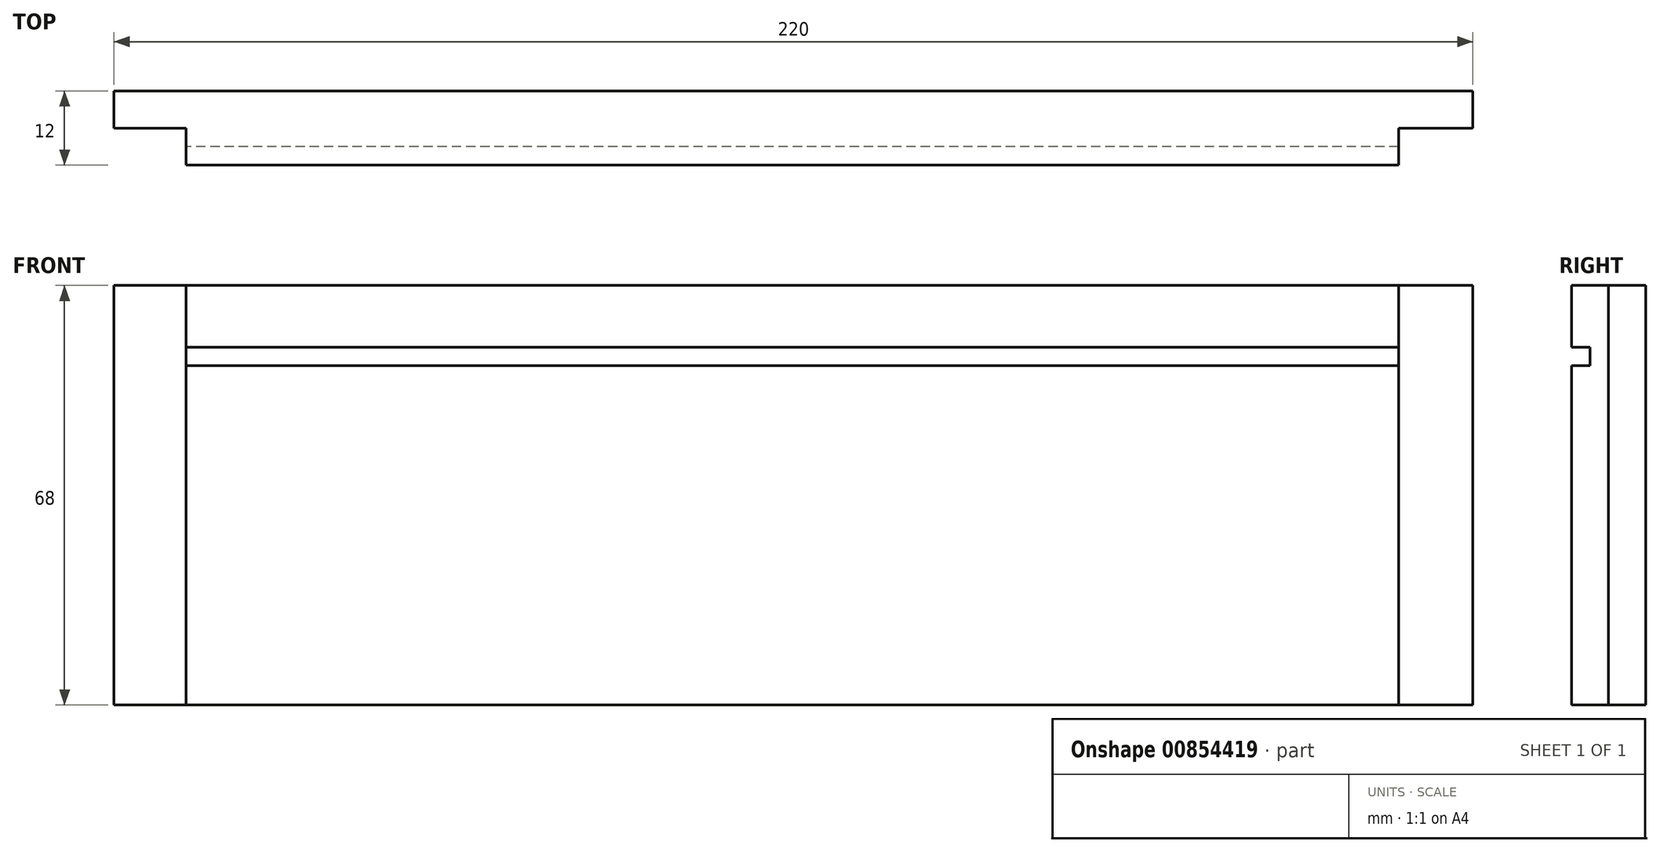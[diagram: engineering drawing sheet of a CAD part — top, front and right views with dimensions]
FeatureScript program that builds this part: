
annotation { "Feature Type Name" : "Feature", "Feature Type Description" : "" }
export const myFeature = defineFeature(function(context is Context, id is Id, definition is map)
    precondition{}
    {
        {
            var Q0;
            Q0=qCreatedBy(makeId("Front.planeOp"),FACE);
            var sketch = newSketch(context, id + "F0", { "sketchPlane" : qUnion([Q0])});
            skLineSegment(sketch, "E0.bottom", {"start": v(-110, 34) * mm, "end": v(110, 34) * mm});
            skLineSegment(sketch, "E0.top", {"start": v(-110, -34) * mm, "end": v(110, -34) * mm});
            skLineSegment(sketch, "E0.left", {"start": v(-110, 34) * mm, "end": v(-110, -34) * mm});
            skLineSegment(sketch, "E0.right", {"start": v(110, 34) * mm, "end": v(110, -34) * mm});
            skPoint(sketch, "E0.middle", {"position": v(0, 0) * mm});
            skSolve(sketch);
        }
        {
            var Q0;
            Q0 = qSketchRegion(id + "F0", true);
            extrude(context, id + "F1", {"entities" : qUnion([Q0]), "depth" : 12 * mm, "offsetDistance" : 25.4 * mm});
        }
        {
            var Q0;
            Q0=makeQuery(id+"F1.opExtrude","SWEPT_FACE",FACE,{"disambiguationData":[OSD([sQuery(id+"F0.wireOp",EDGE,"E0.left")])]});
            var sketch = newSketch(context, id + "F2", { "sketchPlane" : qUnion([Q0])});
            skLineSegment(sketch, "E1.bottom", {"start": v(12, 24) * mm, "end": v(9, 24) * mm});
            skLineSegment(sketch, "E1.top", {"start": v(12, 21) * mm, "end": v(9, 21) * mm});
            skLineSegment(sketch, "E1.left", {"start": v(12, 24) * mm, "end": v(12, 21) * mm});
            skLineSegment(sketch, "E1.right", {"start": v(9, 24) * mm, "end": v(9, 21) * mm});
            skSolve(sketch);
        }
        {
            var Q0;
            Q0 = qSketchRegion(id + "F2", true);
            extrude(context, id + "F3", {"entities" : qUnion([Q0]), "operationType" : NewBodyOperationType.REMOVE, "oppositeDirection" : true, "depth" : 300 * mm, "offsetDistance" : 25.4 * mm});
        }
        {
            var Q0;
            {var subQ0=sQuery(id+"F0.wireOp",EDGE,"E0.top");var subQ1=sQuery(id+"F0.wireOp",EDGE,"E0.left");var subQ2=sQuery(id+"F0.wireOp",EDGE,"E0.right");Q0=makeQuery(id+"F3.boolean.opBoolean","SPLIT",FACE,{"disambiguationData":[TD([makeQuery(id+"F1.opExtrude","SWEPT_FACE",FACE,{"disambiguationData":[OSD([subQ0])]})])],"derivedFrom":makeQuery(id+"F1.opExtrude","CAP_FACE",FACE,{"disambiguationData":[OSD([sQuery(id+"F0.wireOp",EDGE,"E0.bottom"),subQ0,subQ1,subQ2])],"isStart":false})});}
            var sketch = newSketch(context, id + "F4", { "sketchPlane" : qUnion([Q0])});
            skLineSegment(sketch, "E2.bottom", {"start": v(-110.36, 34) * mm, "end": v(-98.36, 34) * mm});
            skLineSegment(sketch, "E2.top", {"start": v(-110.36, -34) * mm, "end": v(-98.36, -34) * mm});
            skLineSegment(sketch, "E2.left", {"start": v(-110.36, 34) * mm, "end": v(-110.36, -34) * mm});
            skLineSegment(sketch, "E2.right", {"start": v(-98.36, 34) * mm, "end": v(-98.36, -34) * mm});
            skLineSegment(sketch, "E3.bottom", {"start": v(110, 34) * mm, "end": v(98, 34) * mm});
            skLineSegment(sketch, "E3.top", {"start": v(110, -34) * mm, "end": v(98, -34) * mm});
            skLineSegment(sketch, "E3.left", {"start": v(110, 34) * mm, "end": v(110, -34) * mm});
            skLineSegment(sketch, "E3.right", {"start": v(98, 34) * mm, "end": v(98, -34) * mm});
            skSolve(sketch);
        }
        {
            var Q0;
            Q0 = qSketchRegion(id + "F4", true);
            extrude(context, id + "F5", {"entities" : qUnion([Q0]), "operationType" : NewBodyOperationType.REMOVE, "oppositeDirection" : true, "depth" : 6 * mm, "offsetDistance" : 25.4 * mm});
        }
    });
